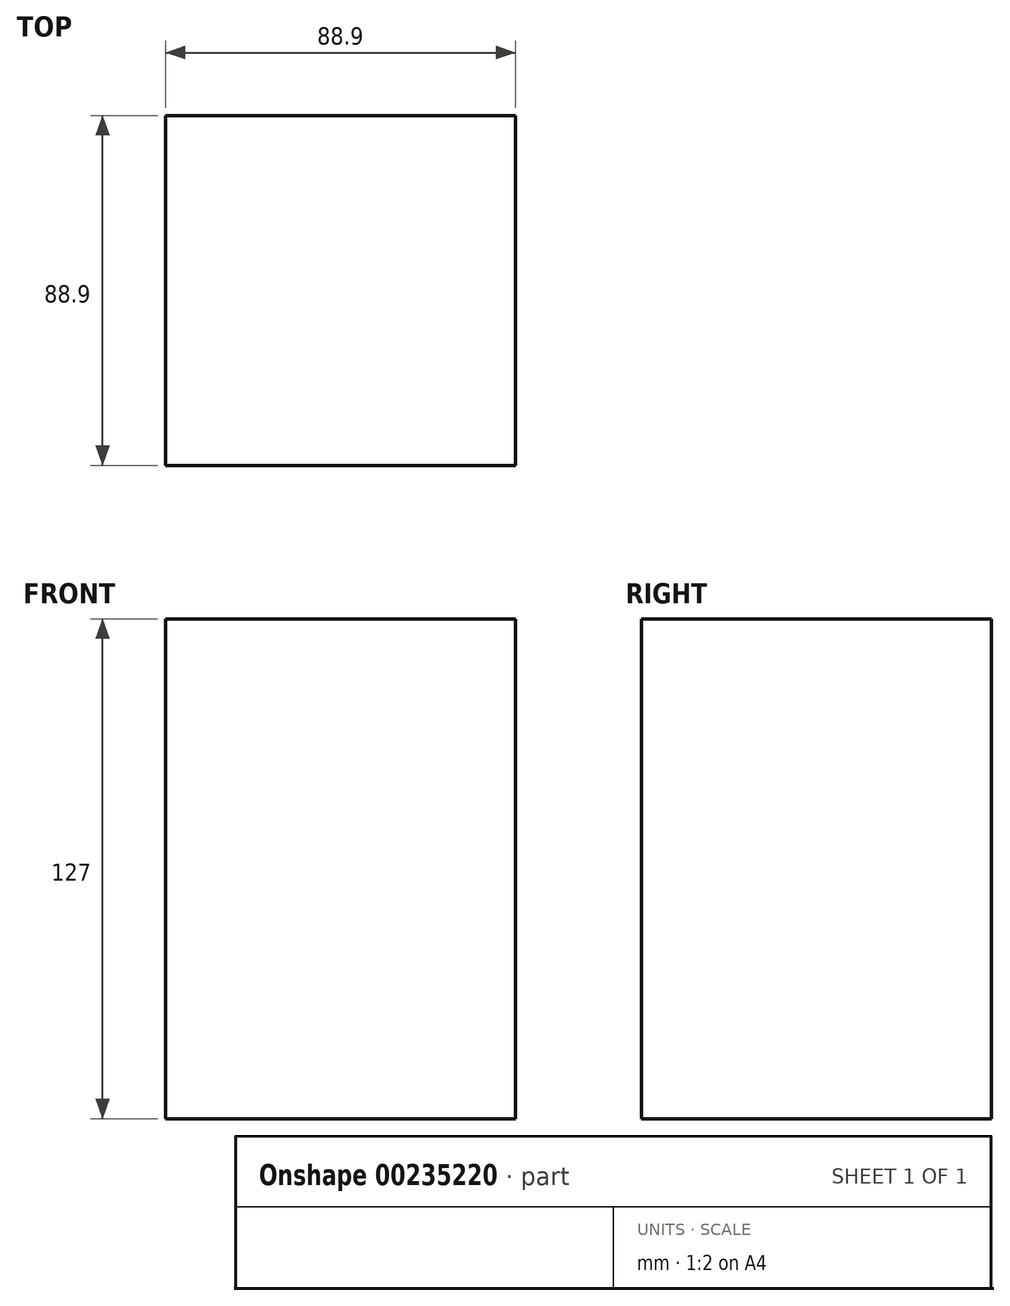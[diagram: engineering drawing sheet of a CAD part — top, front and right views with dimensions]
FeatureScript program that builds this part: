
annotation { "Feature Type Name" : "Feature", "Feature Type Description" : "" }
export const myFeature = defineFeature(function(context is Context, id is Id, definition is map)
    precondition{}
    {
        {
            var Q0;
            Q0=qCreatedBy(makeId("Top.planeOp"),FACE);
            var sketch = newSketch(context, id + "F0", { "sketchPlane" : qUnion([Q0])});
            skLineSegment(sketch, "E0.bottom", {"start": v(0, 0) * mm, "end": v(88.9, 0) * mm});
            skLineSegment(sketch, "E0.top", {"start": v(0, -88.9) * mm, "end": v(88.9, -88.9) * mm});
            skLineSegment(sketch, "E0.left", {"start": v(0, 0) * mm, "end": v(0, -88.9) * mm});
            skLineSegment(sketch, "E0.right", {"start": v(88.9, 0) * mm, "end": v(88.9, -88.9) * mm});
            skSolve(sketch);
        }
        {
            var Q0;
            Q0=makeQuery(id+"F0.imprint","IMPRINT",FACE,{"disambiguationData":[TD([[makeQuery(id+"F0.imprint","IMPRINT",EDGE,{"derivedFrom":sQuery(id+"F0.wireOp",EDGE,"E0.bottom")}),-1.0]])]});
            extrude(context, id + "F1", {"entities" : qUnion([Q0]), "depth" : 127 * mm});
        }
    });
